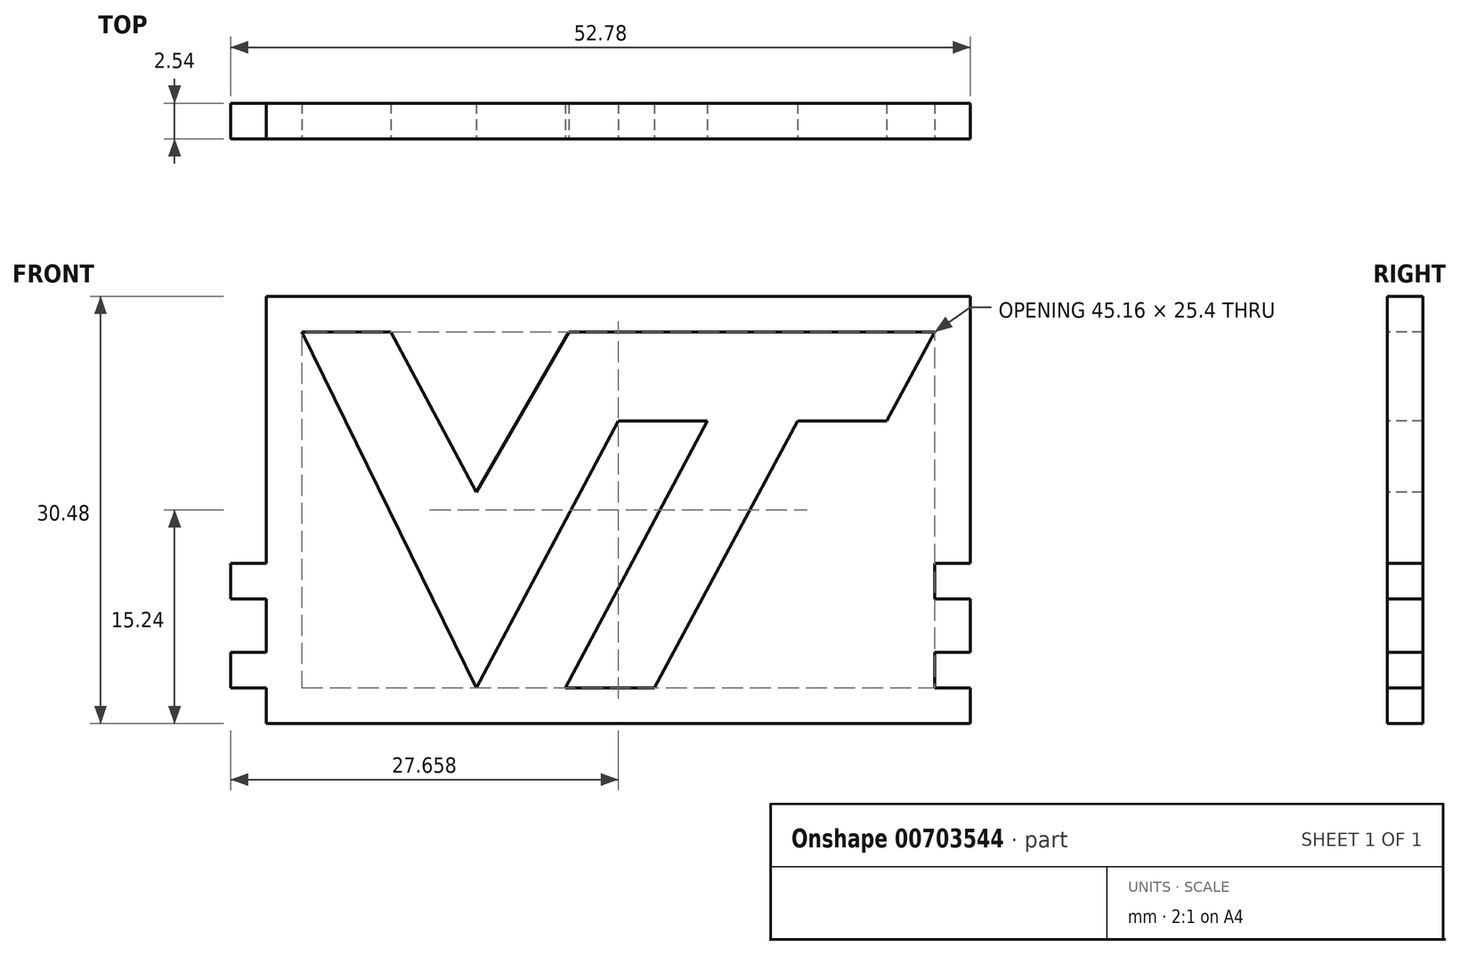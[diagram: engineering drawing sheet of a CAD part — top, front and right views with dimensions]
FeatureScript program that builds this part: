
annotation { "Feature Type Name" : "Feature", "Feature Type Description" : "" }
export const myFeature = defineFeature(function(context is Context, id is Id, definition is map)
    precondition{}
    {
        {
            var Q0;
            Q0=qCreatedBy(makeId("Front.planeOp"),FACE);
            var sketch = newSketch(context, id + "F0", { "sketchPlane" : qUnion([Q0])});
            skLineSegment(sketch, "E0", {"start": v(-15.3, 25.4) * mm, "end": v(-2.83, 0) * mm});
            skLineSegment(sketch, "E1", {"start": v(-2.83, 0) * mm, "end": v(7.28, 19.05) * mm});
            skLineSegment(sketch, "E2", {"start": v(7.28, 19.05) * mm, "end": v(13.63, 19.05) * mm});
            skLineSegment(sketch, "E3", {"start": v(13.63, 19.05) * mm, "end": v(3.52, 0) * mm});
            skLineSegment(sketch, "E4", {"start": v(3.52, 0) * mm, "end": v(9.87, 0) * mm});
            skLineSegment(sketch, "E5", {"start": v(9.87, 0) * mm, "end": v(20.09, 19.05) * mm});
            skLineSegment(sketch, "E6", {"start": v(20.09, 19.05) * mm, "end": v(26.44, 19.05) * mm});
            skLineSegment(sketch, "E7", {"start": v(26.44, 19.05) * mm, "end": v(29.87, 25.4) * mm});
            skLineSegment(sketch, "E8", {"start": v(29.87, 25.4) * mm, "end": v(3.76, 25.4) * mm});
            skLineSegment(sketch, "E9", {"start": v(3.76, 25.4) * mm, "end": v(-2.83, 13.97) * mm});
            skLineSegment(sketch, "E10", {"start": v(-2.83, 13.97) * mm, "end": v(-8.94, 25.4) * mm});
            skLineSegment(sketch, "E11", {"start": v(-8.94, 25.4) * mm, "end": v(-15.3, 25.4) * mm});
            skSolve(sketch);
        }
        {
            var Q0;
            Q0=qCreatedBy(makeId("Front.planeOp"),FACE);
            var sketch = newSketch(context, id + "F1", { "sketchPlane" : qUnion([Q0])});
            skLineSegment(sketch, "E12.bottom", {"start": v(-17.83, 27.94) * mm, "end": v(32.4, 27.94) * mm});
            skLineSegment(sketch, "E12.top", {"start": v(-17.83, -2.54) * mm, "end": v(32.4, -2.54) * mm});
            skLineSegment(sketch, "E12.left", {"start": v(-17.83, 27.94) * mm, "end": v(-17.83, -2.54) * mm});
            skLineSegment(sketch, "E12.right", {"start": v(32.4, 27.94) * mm, "end": v(32.4, -2.54) * mm});
            skSolve(sketch);
        }
        {
            var Q0;
            Q0=makeQuery(id+"F1.imprint","IMPRINT",FACE,{"disambiguationData":[TD([[makeQuery(id+"F1.imprint","IMPRINT",EDGE,{"derivedFrom":sQuery(id+"F1.wireOp",EDGE,"E12.bottom")}),-1.0]])]});
            extrude(context, id + "F2", {"entities" : qUnion([Q0]), "oppositeDirection" : true, "depth" : 2.54 * mm, "offsetDistance" : 25.4 * mm});
        }
        {
            var Q0;
            Q0 = qSketchRegion(id + "F0", true);
            extrude(context, id + "F3", {"entities" : qUnion([Q0]), "operationType" : NewBodyOperationType.REMOVE, "endBound" : BoundingType.UP_TO_NEXT, "oppositeDirection" : true, "depth" : 25.4 * mm, "offsetDistance" : 25.4 * mm});
        }
        {
            var Q0;
            Q0=makeQuery(id+"F1.imprint","IMPRINT",FACE,{"disambiguationData":[TD([[makeQuery(id+"F1.imprint","IMPRINT",EDGE,{"derivedFrom":sQuery(id+"F1.wireOp",EDGE,"E12.bottom")}),-1.0]])]});
            var sketch = newSketch(context, id + "F4", { "sketchPlane" : qUnion([Q0])});
            skLineSegment(sketch, "E13.0.0", {"start": v(-17.83, 27.94) * mm, "end": v(-17.83, -2.54) * mm});
            skLineSegment(sketch, "E13.0.1", {"start": v(-17.83, -2.54) * mm, "end": v(32.4, -2.54) * mm});
            skLineSegment(sketch, "E13.0.2", {"start": v(32.4, -2.54) * mm, "end": v(32.4, 27.94) * mm});
            skLineSegment(sketch, "E13.0.3", {"start": v(32.4, 27.94) * mm, "end": v(-17.83, 27.94) * mm});
            skLineSegment(sketch, "E14.bottom", {"start": v(-17.83, -2.54) * mm, "end": v(-15.3, -2.54) * mm});
            skLineSegment(sketch, "E14.top", {"start": v(-17.83, 11.43) * mm, "end": v(-15.3, 11.43) * mm});
            skLineSegment(sketch, "E14.left", {"start": v(-17.83, -2.54) * mm, "end": v(-17.83, 11.43) * mm});
            skLineSegment(sketch, "E14.right", {"start": v(-15.3, -2.54) * mm, "end": v(-15.3, 11.43) * mm});
            skLineSegment(sketch, "E15.bottom", {"start": v(32.4, -2.54) * mm, "end": v(29.87, -2.54) * mm});
            skLineSegment(sketch, "E15.top", {"start": v(32.4, 12.4) * mm, "end": v(29.87, 12.4) * mm});
            skLineSegment(sketch, "E15.left", {"start": v(32.4, -2.54) * mm, "end": v(32.4, 12.4) * mm});
            skLineSegment(sketch, "E15.right", {"start": v(29.87, -2.54) * mm, "end": v(29.87, 12.4) * mm});
            skLineSegment(sketch, "E16.bottom", {"start": v(-17.83, 6.35) * mm, "end": v(-15.3, 6.35) * mm});
            skLineSegment(sketch, "E16.top", {"start": v(-17.83, 8.9) * mm, "end": v(-15.3, 8.9) * mm});
            skLineSegment(sketch, "E16.left", {"start": v(-17.83, 6.35) * mm, "end": v(-17.83, 8.9) * mm});
            skLineSegment(sketch, "E16.right", {"start": v(-15.3, 6.35) * mm, "end": v(-15.3, 8.9) * mm});
            skLineSegment(sketch, "E17.bottom", {"start": v(-17.83, 0) * mm, "end": v(-15.3, 0) * mm});
            skLineSegment(sketch, "E17.top", {"start": v(-17.83, 2.54) * mm, "end": v(-15.3, 2.54) * mm});
            skLineSegment(sketch, "E17.left", {"start": v(-17.83, 0) * mm, "end": v(-17.83, 2.54) * mm});
            skLineSegment(sketch, "E17.right", {"start": v(-15.3, 0) * mm, "end": v(-15.3, 2.54) * mm});
            skLineSegment(sketch, "E18.bottom", {"start": v(29.87, 6.35) * mm, "end": v(32.4, 6.35) * mm});
            skLineSegment(sketch, "E18.top", {"start": v(29.87, 8.9) * mm, "end": v(32.4, 8.9) * mm});
            skLineSegment(sketch, "E18.left", {"start": v(29.87, 6.35) * mm, "end": v(29.87, 8.9) * mm});
            skLineSegment(sketch, "E18.right", {"start": v(32.4, 6.35) * mm, "end": v(32.4, 8.9) * mm});
            skLineSegment(sketch, "E19.bottom", {"start": v(29.87, 0) * mm, "end": v(32.4, 0) * mm});
            skLineSegment(sketch, "E19.top", {"start": v(29.87, 2.54) * mm, "end": v(32.4, 2.54) * mm});
            skLineSegment(sketch, "E19.left", {"start": v(29.87, 0) * mm, "end": v(29.87, 2.54) * mm});
            skLineSegment(sketch, "E19.right", {"start": v(32.4, 0) * mm, "end": v(32.4, 2.54) * mm});
            skSolve(sketch);
        }
        {
            var Q0;
            Q0=makeQuery(id+"F4.imprint","IMPRINT",FACE,{"disambiguationData":[TD([[makeQuery(id+"F4.imprint","IMPRINT",EDGE,{"derivedFrom":sQuery(id+"F4.wireOp",EDGE,"E18.bottom")}),1.0]])]});
            var Q1;
            Q1=makeQuery(id+"F4.imprint","IMPRINT",FACE,{"disambiguationData":[TD([[makeQuery(id+"F4.imprint","IMPRINT",EDGE,{"derivedFrom":sQuery(id+"F4.wireOp",EDGE,"E19.bottom")}),1.0]])]});
            extrude(context, id + "F5", {"entities" : qUnion([Q0, Q1]), "operationType" : NewBodyOperationType.REMOVE, "endBound" : BoundingType.UP_TO_NEXT, "oppositeDirection" : true, "depth" : 25.4 * mm, "offsetDistance" : 25.4 * mm});
        }
        {
            var Q0;
            Q0=makeQuery(id+"F2.opExtrude","SWEPT_FACE",FACE,{"disambiguationData":[OSD([sQuery(id+"F1.wireOp",EDGE,"E12.left")])]});
            var sketch = newSketch(context, id + "F6", { "sketchPlane" : qUnion([Q0])});
            skLineSegment(sketch, "E20.bottom", {"start": v(-2.54, -2.54) * mm, "end": v(0, -2.54) * mm});
            skLineSegment(sketch, "E20.top", {"start": v(-2.54, 11.43) * mm, "end": v(0, 11.43) * mm});
            skLineSegment(sketch, "E20.left", {"start": v(-2.54, -2.54) * mm, "end": v(-2.54, 11.43) * mm});
            skLineSegment(sketch, "E20.right", {"start": v(0, -2.54) * mm, "end": v(0, 11.43) * mm});
            skLineSegment(sketch, "E21.bottom", {"start": v(-2.54, 8.9) * mm, "end": v(0, 8.9) * mm});
            skLineSegment(sketch, "E21.top", {"start": v(-2.54, 6.35) * mm, "end": v(0, 6.35) * mm});
            skLineSegment(sketch, "E21.left", {"start": v(-2.54, 8.9) * mm, "end": v(-2.54, 6.35) * mm});
            skLineSegment(sketch, "E21.right", {"start": v(0, 8.9) * mm, "end": v(0, 6.35) * mm});
            skLineSegment(sketch, "E22.bottom", {"start": v(-2.54, 2.54) * mm, "end": v(0, 2.54) * mm});
            skLineSegment(sketch, "E22.top", {"start": v(-2.54, 0) * mm, "end": v(0, 0) * mm});
            skLineSegment(sketch, "E22.left", {"start": v(-2.54, 2.54) * mm, "end": v(-2.54, 0) * mm});
            skLineSegment(sketch, "E22.right", {"start": v(0, 2.54) * mm, "end": v(0, 0) * mm});
            skSolve(sketch);
        }
        {
            var Q0;
            Q0=makeQuery(id+"F6.imprint","IMPRINT",FACE,{"disambiguationData":[TD([[makeQuery(id+"F6.imprint","IMPRINT",EDGE,{"derivedFrom":sQuery(id+"F6.wireOp",EDGE,"E21.bottom")}),-1.0]])]});
            var Q1;
            Q1=makeQuery(id+"F6.imprint","IMPRINT",FACE,{"disambiguationData":[TD([[makeQuery(id+"F6.imprint","IMPRINT",EDGE,{"derivedFrom":sQuery(id+"F6.wireOp",EDGE,"E22.bottom")}),-1.0]])]});
            extrude(context, id + "F7", {"entities" : qUnion([Q0, Q1]), "operationType" : NewBodyOperationType.ADD, "depth" : 2.54 * mm, "offsetDistance" : 25.4 * mm});
        }
    });
